# Revit family: PL200
name_source: partatom
category: Lighting Fixtures
units: mm (PartAtom-declared; Revit-internal decimal feet)

## family parameters
Cut with Voids When Loaded = No
Host = Face
Light Source = Yes
Maintain Annotation Orientation = No
Part Type = Normal
Room Calculation Point = No
Round Connector Dimension = Use Diameter
Shared = No

## types (1)
- PL200
    CAP = Yes
    Color Filter = 16777215
    Concrete Pour Box Depth = -1' - 1"
    Concrete Pour Box Dia = 0' - 8 1/8"
    Cutout = 0' - 3 3/4"
    Default Elevation = 4' - 0"
    Description = PATH LIGHT
    Dimming Lamp Color Temperature Shift = <None>
    Emit from Line Length = 2' - 0"
    Light Source Symbol Length = 10' - 0"
    Manufacturer = LUMUX
    Model = PL200
    Radius = 0' - 4 3/4"
    Spot Beam Angle = 30.00°
    Spot Field Angle = 90.00°
    Tilt Angle = 90.00°
    URL = https://cdn.shopify.com

## geometry (parser evidence)
native form markers: Sweep x3
no freeform markers — native parametric forms only
